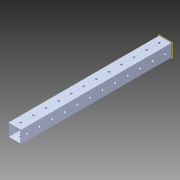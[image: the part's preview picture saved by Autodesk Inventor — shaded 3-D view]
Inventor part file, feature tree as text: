
AUTODESK INVENTOR PART (.ipt)
format: ipt  version: 2014 (Build 180170000, 170)  size: 1,206,272 bytes
history: native  units: in
note: dims shown in document units (in); Inventor stores cm internally (conversion verified against a paired STEP export)
features: pattern_circular x1, other x1, plane x1, extrude x1, imported_body x1, sketch x1
ambient origin geometry x8: Origin, YZ Plane, XZ Plane, XY Plane, X Axis, Y Axis, Z Axis, Center Point
bodies: Body1 (feature_tree)
feature tree (6):
  pattern_circular  "CirPattern2"
  other  "217-3426-STEP1"
  plane  "Work Plane1"
  extrude  "Extrusion1"  Depth=3937.0079in TaperAngle=0.0deg
  imported_body  "Base1"
  sketch  "Sketch1"  dims[d0=-12.0in d1=3937.0079in d2=0.0in]
